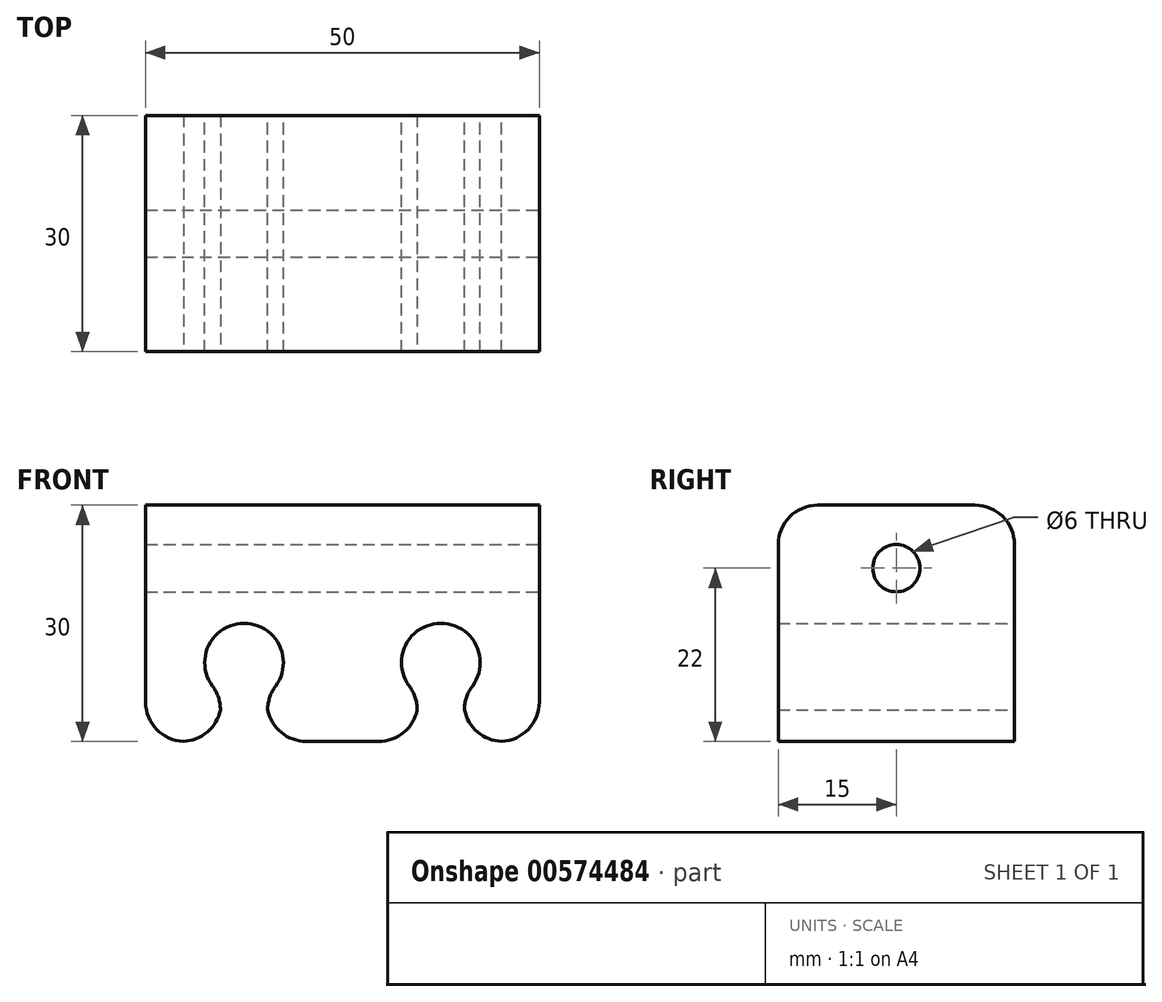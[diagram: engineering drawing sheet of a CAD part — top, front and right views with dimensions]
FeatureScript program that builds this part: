
annotation { "Feature Type Name" : "Feature", "Feature Type Description" : "" }
export const myFeature = defineFeature(function(context is Context, id is Id, definition is map)
    precondition{}
    {
        {
            var Q0;
            Q0=qCreatedBy(makeId("Front.planeOp"),FACE);
            var sketch = newSketch(context, id + "F0", { "sketchPlane" : qUnion([Q0])});
            skLineSegment(sketch, "E0.bottom", {"start": v(0, 0) * mm, "end": v(50, 0) * mm});
            skLineSegment(sketch, "E0.top", {"start": v(0, 30) * mm, "end": v(50, 30) * mm});
            skLineSegment(sketch, "E0.left", {"start": v(0, 0) * mm, "end": v(0, 30) * mm});
            skLineSegment(sketch, "E0.right", {"start": v(50, 0) * mm, "end": v(50, 30) * mm});
            skPoint(sketch, "E1", {"position": v(12.5, 10) * mm});
            skPoint(sketch, "E2", {"position": v(37.5, 10) * mm});
            skCircle(sketch, "E3", {"center": v(12.5, 10) * mm, "radius": 5 * mm});
            skCircle(sketch, "E4", {"center": v(37.5, 10) * mm, "radius": 5 * mm});
            skLineSegment(sketch, "E5.bottom", {"start": v(9.5, 0) * mm, "end": v(15.5, 0) * mm});
            skLineSegment(sketch, "E5.top", {"start": v(9.5, 6) * mm, "end": v(15.5, 6) * mm});
            skLineSegment(sketch, "E5.left", {"start": v(9.5, 0) * mm, "end": v(9.5, 6) * mm});
            skLineSegment(sketch, "E5.right", {"start": v(15.5, 0) * mm, "end": v(15.5, 6) * mm});
            skLineSegment(sketch, "E6.bottom", {"start": v(34.5, 0) * mm, "end": v(40.5, 0) * mm});
            skLineSegment(sketch, "E6.top", {"start": v(34.5, 6) * mm, "end": v(40.5, 6) * mm});
            skLineSegment(sketch, "E6.left", {"start": v(34.5, 0) * mm, "end": v(34.5, 6) * mm});
            skLineSegment(sketch, "E6.right", {"start": v(40.5, 0) * mm, "end": v(40.5, 6) * mm});
            skSolve(sketch);
        }
        {
            var Q0;
            Q0=makeQuery(id+"F0.imprint","IMPRINT",FACE,{"disambiguationData":[TD([[makeQuery(id+"F0.imprint","IMPRINT",EDGE,{"derivedFrom":sQuery(id+"F0.wireOp",EDGE,"E0.top")}),-1.0]])]});
            extrude(context, id + "F1", {"entities" : qUnion([Q0]), "depth" : 30 * mm, "offsetDistance" : 25 * mm});
        }
        {
            var Q0;
            Q0=makeQuery(id+"F1.opExtrude","SWEPT_EDGE",EDGE,{"disambiguationData":[OSD([sQuery(id+"F0.wireOp",EDGE,"E4"),sQuery(id+"F0.wireOp",EDGE,"E6.top"),sQuery(id+"F0.wireOp",EDGE,"E6.right")])]});
            var Q1;
            Q1=makeQuery(id+"F1.opExtrude","SWEPT_EDGE",EDGE,{"disambiguationData":[OSD([sQuery(id+"F0.wireOp",EDGE,"E4"),sQuery(id+"F0.wireOp",EDGE,"E6.top"),sQuery(id+"F0.wireOp",EDGE,"E6.left")])]});
            var Q2;
            Q2=makeQuery(id+"F1.opExtrude","SWEPT_EDGE",EDGE,{"disambiguationData":[OSD([sQuery(id+"F0.wireOp",EDGE,"E3"),sQuery(id+"F0.wireOp",EDGE,"E5.top"),sQuery(id+"F0.wireOp",EDGE,"E5.left")])]});
            var Q3;
            Q3=makeQuery(id+"F1.opExtrude","SWEPT_EDGE",EDGE,{"disambiguationData":[OSD([sQuery(id+"F0.wireOp",EDGE,"E3"),sQuery(id+"F0.wireOp",EDGE,"E5.top"),sQuery(id+"F0.wireOp",EDGE,"E5.right")])]});
            fillet(context, id + "F2", {"entities" : qUnion([Q0, Q1, Q2, Q3]), "radius" : 5 * mm, "tangentPropagation" : true, "allowEdgeOverflow" : false});
        }
        {
            var Q0;
            Q0=makeQuery(id+"F1.opExtrude","SWEPT_EDGE",EDGE,{"disambiguationData":[OSD([sQuery(id+"F0.wireOp",EDGE,"E0.bottom"),sQuery(id+"F0.wireOp",EDGE,"E5.bottom"),sQuery(id+"F0.wireOp",EDGE,"E5.left")])]});
            var Q1;
            Q1=makeQuery(id+"F1.opExtrude","SWEPT_EDGE",EDGE,{"disambiguationData":[OSD([sQuery(id+"F0.wireOp",EDGE,"E0.bottom"),sQuery(id+"F0.wireOp",EDGE,"E6.bottom"),sQuery(id+"F0.wireOp",EDGE,"E6.left")])]});
            var Q2;
            Q2=makeQuery(id+"F1.opExtrude","SWEPT_EDGE",EDGE,{"disambiguationData":[OSD([sQuery(id+"F0.wireOp",EDGE,"E0.bottom"),sQuery(id+"F0.wireOp",EDGE,"E0.right")])]});
            var Q3;
            Q3=makeQuery(id+"F1.opExtrude","SWEPT_EDGE",EDGE,{"disambiguationData":[OSD([sQuery(id+"F0.wireOp",EDGE,"E0.bottom"),sQuery(id+"F0.wireOp",EDGE,"E6.bottom"),sQuery(id+"F0.wireOp",EDGE,"E6.right")])]});
            var Q4;
            Q4=makeQuery(id+"F1.opExtrude","SWEPT_EDGE",EDGE,{"disambiguationData":[OSD([sQuery(id+"F0.wireOp",EDGE,"E0.bottom"),sQuery(id+"F0.wireOp",EDGE,"E0.left")])]});
            var Q5;
            Q5=makeQuery(id+"F1.opExtrude","SWEPT_EDGE",EDGE,{"disambiguationData":[OSD([sQuery(id+"F0.wireOp",EDGE,"E0.bottom"),sQuery(id+"F0.wireOp",EDGE,"E5.bottom"),sQuery(id+"F0.wireOp",EDGE,"E5.right")])]});
            fillet(context, id + "F3", {"entities" : qUnion([Q0, Q1, Q2, Q3, Q4, Q5]), "radius" : 5 * mm, "tangentPropagation" : true, "allowEdgeOverflow" : false});
        }
        {
            var Q0;
            Q0=makeQuery(id+"F1.opExtrude","CAP_EDGE",EDGE,{"disambiguationData":[OSD([sQuery(id+"F0.wireOp",EDGE,"E0.top")])],"isStart":false});
            var Q1;
            Q1=makeQuery(id+"F1.opExtrude","CAP_EDGE",EDGE,{"disambiguationData":[OSD([sQuery(id+"F0.wireOp",EDGE,"E0.top")])],"isStart":true});
            fillet(context, id + "F4", {"entities" : qUnion([Q0, Q1]), "radius" : 5 * mm, "tangentPropagation" : true, "allowEdgeOverflow" : false});
        }
        {
            var Q0;
            Q0=makeQuery(id+"F1.opExtrude","SWEPT_FACE",FACE,{"disambiguationData":[OSD([sQuery(id+"F0.wireOp",EDGE,"E0.right")])]});
            var sketch = newSketch(context, id + "F5", { "sketchPlane" : qUnion([Q0])});
            skPoint(sketch, "E7", {"position": v(-15, 22) * mm});
            skSolve(sketch);
        }
        {
            var Q0;
            Q0=sQuery(id+"F5.wireOp",VERTEX,"E7");
            var Q1;
            Q1=makeQuery(id+"F1.opExtrude","SWEPT_BODY",BODY,{"disambiguationData":[OSD([sQuery(id+"F0.wireOp",EDGE,"E0.bottom"),sQuery(id+"F0.wireOp",EDGE,"E0.top"),sQuery(id+"F0.wireOp",EDGE,"E0.left"),sQuery(id+"F0.wireOp",EDGE,"E0.right"),sQuery(id+"F0.wireOp",EDGE,"E3"),sQuery(id+"F0.wireOp",EDGE,"E4"),sQuery(id+"F0.wireOp",EDGE,"E5.left"),sQuery(id+"F0.wireOp",EDGE,"E5.right"),sQuery(id+"F0.wireOp",EDGE,"E6.left"),sQuery(id+"F0.wireOp",EDGE,"E6.right")])]});
            hole(context, id + "F6", {"style" : HoleStyle.SIMPLE, "endStyle" : HoleEndStyle.THROUGH, "holeDiameter" : 6 * mm, "isTappedThrough" : true, "tappedDepth" : 12 * mm, "tapClearance" : 3, "locations" : qUnion([Q0]), "scope" : qUnion([Q1])});
        }
    });
